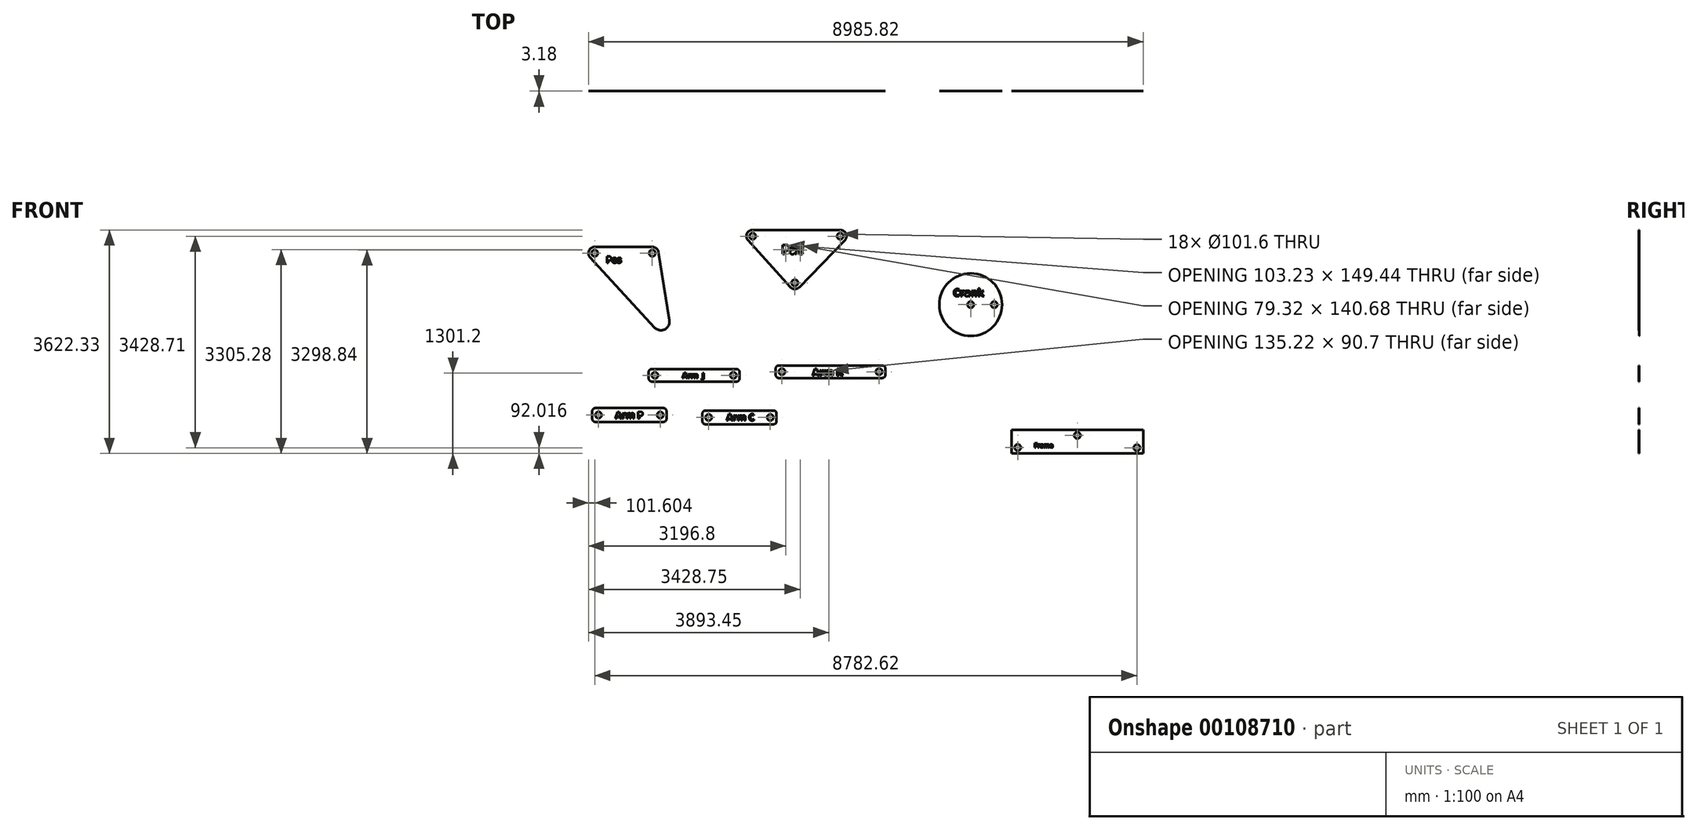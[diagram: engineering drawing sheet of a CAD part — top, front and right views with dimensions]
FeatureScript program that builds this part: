
annotation { "Feature Type Name" : "Feature", "Feature Type Description" : "" }
export const myFeature = defineFeature(function(context is Context, id is Id, definition is map)
    precondition{}
    {
        {
            var Q0;
            Q0=qCreatedBy(makeId("Front.planeOp"),FACE);
            var sketch = newSketch(context, id + "F0", { "sketchPlane" : qUnion([Q0])});
            skLineSegment(sketch, "E0", {"start": v(-44.34, 0) * mm, "end": v(-241.1, 1228.95) * mm, "construction": true});
            skLineSegment(sketch, "E1", {"start": v(-241.1, 1228.95) * mm, "end": v(-1173.29, 1228.95) * mm, "construction": true});
            skLineSegment(sketch, "E2", {"start": v(-1173.29, 1228.95) * mm, "end": v(-44.34, 0) * mm, "construction": true});
            skLineSegment(sketch, "E3", {"start": v(-140.78, 1245.01) * mm, "end": v(35.95, 141.16) * mm});
            skLineSegment(sketch, "E4", {"start": v(-241.1, 1330.55) * mm, "end": v(-1173.29, 1330.55) * mm});
            skLineSegment(sketch, "E5", {"start": v(-1248.1, 1160.21) * mm, "end": v(-204.87, 24.57) * mm});
            skCircle(sketch, "E6", {"center": v(-1173.29, 1228.95) * mm, "radius": 50.8 * mm});
            skCircle(sketch, "E7", {"center": v(-241.1, 1228.95) * mm, "radius": 50.8 * mm});
            skPoint(sketch, "E8.visualSharp", {"position": v(-1404.58, 1330.55) * mm});
            skArc(sketch, "E8.filletArc", {"start": v(-1173.29, 1330.55) * mm, "mid": v(-1266.3, 1269.8) * mm, "end": v(-1248.1, 1160.21) * mm});
            skPoint(sketch, "E9.visualSharp", {"position": v(-154.48, 1330.55) * mm});
            skArc(sketch, "E9.filletArc", {"start": v(-140.78, 1245.01) * mm, "mid": v(-175.19, 1306.26) * mm, "end": v(-241.1, 1330.55) * mm});
            skPoint(sketch, "E10.visualSharp", {"position": v(109.4, -317.53) * mm});
            skArc(sketch, "E10.filletArc", {"start": v(-204.87, 24.57) * mm, "mid": v(-41.12, -6.66) * mm, "end": v(35.95, 141.16) * mm});
            skText(sketch, "E11", { "text": "Pes", "fontName": "OpenSans-Bold.ttf"});
            const initialGuessF0  = {"E11": [-0.98944, 1.07226, 1, 0, 0.10494]};
            skSetInitialGuess(sketch, initialGuessF0);
            skSolve(sketch);
        }
        {
            var Q0;
            Q0=makeQuery(id+"F0.imprint","IMPRINT",FACE,{"disambiguationData":[TD([[makeQuery(id+"F0.imprint","IMPRINT",EDGE,{"derivedFrom":sQuery(id+"F0.wireOp",EDGE,"E3")}),-1.0]])]});
            extrude(context, id + "F1", {"entities" : qUnion([Q0]), "depth" : 3.17 * mm});
        }
        {
            var Q0;
            Q0=qCreatedBy(makeId("Front.planeOp"),FACE);
            var sketch = newSketch(context, id + "F2", { "sketchPlane" : qUnion([Q0])});
            skLineSegment(sketch, "E12", {"start": v(2067.64, 748.14) * mm, "end": v(2802.3, 1504.05) * mm, "construction": true});
            skLineSegment(sketch, "E13", {"start": v(2802.3, 1504.05) * mm, "end": v(1384.98, 1504.05) * mm, "construction": true});
            skLineSegment(sketch, "E14", {"start": v(1384.98, 1504.05) * mm, "end": v(2067.64, 748.14) * mm, "construction": true});
            skLineSegment(sketch, "E15", {"start": v(2875.16, 1433.24) * mm, "end": v(2140.5, 677.33) * mm});
            skLineSegment(sketch, "E16", {"start": v(2802.3, 1605.65) * mm, "end": v(1384.98, 1605.65) * mm});
            skLineSegment(sketch, "E17", {"start": v(1309.58, 1435.95) * mm, "end": v(1992.24, 680.04) * mm});
            skCircle(sketch, "E18", {"center": v(1384.98, 1504.05) * mm, "radius": 50.8 * mm});
            skCircle(sketch, "E19", {"center": v(2802.3, 1504.05) * mm, "radius": 50.8 * mm});
            skPoint(sketch, "E20.visualSharp", {"position": v(1156.33, 1605.65) * mm});
            skArc(sketch, "E20.filletArc", {"start": v(1384.98, 1605.65) * mm, "mid": v(1292.14, 1545.3) * mm, "end": v(1309.58, 1435.95) * mm});
            skPoint(sketch, "E21.visualSharp", {"position": v(3042.73, 1605.65) * mm});
            skArc(sketch, "E21.filletArc", {"start": v(2875.16, 1433.24) * mm, "mid": v(2895.89, 1543.6) * mm, "end": v(2802.3, 1605.65) * mm});
            skPoint(sketch, "E22.visualSharp", {"position": v(2064.92, 599.56) * mm});
            skArc(sketch, "E22.filletArc", {"start": v(1992.24, 680.04) * mm, "mid": v(2065.78, 646.56) * mm, "end": v(2140.5, 677.33) * mm});
            skCircle(sketch, "E23", {"center": v(2067.64, 748.14) * mm, "radius": 50.8 * mm});
            skText(sketch, "E24", { "text": "Pat", "fontName": "OpenSans-Bold.ttf"});
            const initialGuessF2  = {"E24": [1.85149, 1.21388, 1, 0, 0.15072]};
            skSetInitialGuess(sketch, initialGuessF2);
            skSolve(sketch);
        }
        {
            var Q0;
            Q0=makeQuery(id+"F2.imprint","IMPRINT",FACE,{"disambiguationData":[TD([[makeQuery(id+"F2.imprint","IMPRINT",EDGE,{"derivedFrom":sQuery(id+"F2.wireOp",EDGE,"E15")}),-1.0]])]});
            extrude(context, id + "F3", {"entities" : qUnion([Q0]), "depth" : 3.17 * mm});
        }
        {
            var Q0;
            Q0=qCreatedBy(makeId("Front.planeOp"),FACE);
            var sketch = newSketch(context, id + "F4", { "sketchPlane" : qUnion([Q0])});
            skLineSegment(sketch, "E25.bottom", {"start": v(-248.2, -648.94) * mm, "end": v(1123.4, -648.94) * mm});
            skLineSegment(sketch, "E25.top", {"start": v(-248.2, -852.14) * mm, "end": v(1123.4, -852.14) * mm});
            skLineSegment(sketch, "E25.left", {"start": v(-299, -699.74) * mm, "end": v(-299, -801.34) * mm});
            skLineSegment(sketch, "E25.right", {"start": v(1174.2, -699.74) * mm, "end": v(1174.2, -801.34) * mm});
            skLineSegment(sketch, "E26", {"start": v(-197.4, -750.54) * mm, "end": v(1072.6, -750.54) * mm, "construction": true});
            skPoint(sketch, "E26.startSnap0", {"position": v(-299, -750.54) * mm});
            skPoint(sketch, "E26.endSnap0", {"position": v(1174.2, -750.54) * mm});
            skCircle(sketch, "E27", {"center": v(-197.4, -750.54) * mm, "radius": 50.8 * mm});
            skCircle(sketch, "E28", {"center": v(1072.6, -750.54) * mm, "radius": 50.8 * mm});
            skPoint(sketch, "E29.visualSharp", {"position": v(1174.2, -852.14) * mm});
            skArc(sketch, "E29.filletArc", {"start": v(1123.4, -852.14) * mm, "mid": v(1159.32, -837.26) * mm, "end": v(1174.2, -801.34) * mm});
            skPoint(sketch, "E30.visualSharp", {"position": v(1174.2, -648.94) * mm});
            skArc(sketch, "E30.filletArc", {"start": v(1174.2, -699.74) * mm, "mid": v(1159.32, -663.82) * mm, "end": v(1123.4, -648.94) * mm});
            skPoint(sketch, "E31.visualSharp", {"position": v(-299, -648.94) * mm});
            skArc(sketch, "E31.filletArc", {"start": v(-248.2, -648.94) * mm, "mid": v(-284.13, -663.82) * mm, "end": v(-299, -699.74) * mm});
            skPoint(sketch, "E32.visualSharp", {"position": v(-299, -852.14) * mm});
            skArc(sketch, "E32.filletArc", {"start": v(-299, -801.34) * mm, "mid": v(-284.13, -837.26) * mm, "end": v(-248.2, -852.14) * mm});
            skText(sketch, "E33", { "text": "Arm  J", "fontName": "OpenSans-Bold.ttf"});
            const initialGuessF4  = {"E33": [0.24657, -0.79744, 1, 0, 0.08674]};
            skSetInitialGuess(sketch, initialGuessF4);
            skSolve(sketch);
        }
        {
            var Q0;
            Q0=makeQuery(id+"F4.imprint","IMPRINT",FACE,{"disambiguationData":[TD([[makeQuery(id+"F4.imprint","IMPRINT",EDGE,{"derivedFrom":sQuery(id+"F4.wireOp",EDGE,"E25.bottom")}),-1.0]])]});
            extrude(context, id + "F5", {"entities" : qUnion([Q0]), "depth" : 3.17 * mm});
        }
        {
            var Q0;
            Q0=qCreatedBy(makeId("Front.planeOp"),FACE);
            var sketch = newSketch(context, id + "F6", { "sketchPlane" : qUnion([Q0])});
            skLineSegment(sketch, "E34.bottom", {"start": v(1808.96, -591.1) * mm, "end": v(3482.82, -591.1) * mm});
            skLineSegment(sketch, "E34.top", {"start": v(1808.96, -794.3) * mm, "end": v(3482.82, -794.3) * mm});
            skLineSegment(sketch, "E34.left", {"start": v(1758.16, -641.9) * mm, "end": v(1758.16, -743.5) * mm});
            skLineSegment(sketch, "E34.right", {"start": v(3533.62, -641.9) * mm, "end": v(3533.62, -743.5) * mm});
            skLineSegment(sketch, "E35", {"start": v(1859.76, -692.7) * mm, "end": v(3432.02, -692.7) * mm, "construction": true});
            skPoint(sketch, "E35.startSnap0", {"position": v(1758.16, -692.7) * mm});
            skPoint(sketch, "E35.endSnap0", {"position": v(3533.62, -692.7) * mm});
            skCircle(sketch, "E36", {"center": v(1859.76, -692.7) * mm, "radius": 50.8 * mm});
            skCircle(sketch, "E37", {"center": v(3432.02, -692.7) * mm, "radius": 50.8 * mm});
            skPoint(sketch, "E38.visualSharp", {"position": v(3533.62, -794.3) * mm});
            skArc(sketch, "E38.filletArc", {"start": v(3482.82, -794.3) * mm, "mid": v(3518.74, -779.42) * mm, "end": v(3533.62, -743.5) * mm});
            skPoint(sketch, "E39.visualSharp", {"position": v(3533.62, -591.1) * mm});
            skArc(sketch, "E39.filletArc", {"start": v(3533.62, -641.9) * mm, "mid": v(3518.74, -605.98) * mm, "end": v(3482.82, -591.1) * mm});
            skPoint(sketch, "E40.visualSharp", {"position": v(1758.16, -591.1) * mm});
            skArc(sketch, "E40.filletArc", {"start": v(1808.96, -591.1) * mm, "mid": v(1773.04, -605.98) * mm, "end": v(1758.16, -641.9) * mm});
            skPoint(sketch, "E41.visualSharp", {"position": v(1758.16, -794.3) * mm});
            skArc(sketch, "E41.filletArc", {"start": v(1758.16, -743.5) * mm, "mid": v(1773.04, -779.42) * mm, "end": v(1808.96, -794.3) * mm});
            skText(sketch, "E42", { "text": "Arm K", "fontName": "OpenSans-Bold.ttf"});
            const initialGuessF6  = {"E42": [2.35162, -0.76083, 1, 0, 0.11743]};
            skSetInitialGuess(sketch, initialGuessF6);
            skSolve(sketch);
        }
        {
            var Q0;
            Q0=qCreatedBy(makeId("Front.planeOp"),FACE);
            var sketch = newSketch(context, id + "F7", { "sketchPlane" : qUnion([Q0])});
            skLineSegment(sketch, "E43.bottom", {"start": v(-1163, -1282.62) * mm, "end": v(-60.65, -1282.62) * mm});
            skLineSegment(sketch, "E43.top", {"start": v(-1163, -1506.74) * mm, "end": v(-60.65, -1506.74) * mm});
            skLineSegment(sketch, "E43.left", {"start": v(-1213.8, -1333.42) * mm, "end": v(-1213.8, -1455.94) * mm});
            skLineSegment(sketch, "E43.right", {"start": v(-9.85, -1333.42) * mm, "end": v(-9.85, -1455.94) * mm});
            skLineSegment(sketch, "E44", {"start": v(-1112.2, -1394.68) * mm, "end": v(-111.45, -1394.68) * mm, "construction": true});
            skPoint(sketch, "E44.startSnap0", {"position": v(-1213.8, -1394.68) * mm});
            skPoint(sketch, "E44.endSnap0", {"position": v(-9.85, -1394.68) * mm});
            skCircle(sketch, "E45", {"center": v(-1112.2, -1394.68) * mm, "radius": 50.8 * mm});
            skCircle(sketch, "E46", {"center": v(-111.45, -1394.68) * mm, "radius": 50.8 * mm});
            skPoint(sketch, "E47.visualSharp", {"position": v(-9.85, -1506.74) * mm});
            skArc(sketch, "E47.filletArc", {"start": v(-60.65, -1506.74) * mm, "mid": v(-24.73, -1491.86) * mm, "end": v(-9.85, -1455.94) * mm});
            skPoint(sketch, "E48.visualSharp", {"position": v(-9.85, -1282.62) * mm});
            skArc(sketch, "E48.filletArc", {"start": v(-9.85, -1333.42) * mm, "mid": v(-24.73, -1297.5) * mm, "end": v(-60.65, -1282.62) * mm});
            skPoint(sketch, "E49.visualSharp", {"position": v(-1213.8, -1282.62) * mm});
            skArc(sketch, "E49.filletArc", {"start": v(-1163, -1282.62) * mm, "mid": v(-1198.93, -1297.5) * mm, "end": v(-1213.8, -1333.42) * mm});
            skPoint(sketch, "E50.visualSharp", {"position": v(-1213.8, -1506.74) * mm});
            skArc(sketch, "E50.filletArc", {"start": v(-1213.8, -1455.94) * mm, "mid": v(-1198.93, -1491.86) * mm, "end": v(-1163, -1506.74) * mm});
            skText(sketch, "E51", { "text": "Arm P", "fontName": "OpenSans-Bold.ttf"});
            const initialGuessF7  = {"E51": [-0.84316, -1.44791, 1, 0, 0.10851]};
            skSetInitialGuess(sketch, initialGuessF7);
            skSolve(sketch);
        }
        {
            var Q0;
            Q0=qCreatedBy(makeId("Front.planeOp"),FACE);
            var sketch = newSketch(context, id + "F8", { "sketchPlane" : qUnion([Q0])});
            skLineSegment(sketch, "E52.bottom", {"start": v(621.11, -1321.32) * mm, "end": v(1720.93, -1321.32) * mm});
            skLineSegment(sketch, "E52.top", {"start": v(621.11, -1545.44) * mm, "end": v(1720.93, -1545.44) * mm});
            skLineSegment(sketch, "E52.left", {"start": v(570.31, -1372.12) * mm, "end": v(570.31, -1494.64) * mm});
            skLineSegment(sketch, "E52.right", {"start": v(1771.73, -1372.12) * mm, "end": v(1771.73, -1494.64) * mm});
            skLineSegment(sketch, "E53", {"start": v(671.91, -1433.38) * mm, "end": v(1670.13, -1433.38) * mm, "construction": true});
            skPoint(sketch, "E53.startSnap0", {"position": v(570.31, -1433.38) * mm});
            skPoint(sketch, "E53.endSnap0", {"position": v(1771.73, -1433.38) * mm});
            skCircle(sketch, "E54", {"center": v(671.91, -1433.38) * mm, "radius": 50.8 * mm});
            skCircle(sketch, "E55", {"center": v(1670.13, -1433.38) * mm, "radius": 50.8 * mm});
            skPoint(sketch, "E56.visualSharp", {"position": v(1771.73, -1545.44) * mm});
            skArc(sketch, "E56.filletArc", {"start": v(1720.93, -1545.44) * mm, "mid": v(1756.85, -1530.56) * mm, "end": v(1771.73, -1494.64) * mm});
            skPoint(sketch, "E57.visualSharp", {"position": v(1771.73, -1321.32) * mm});
            skArc(sketch, "E57.filletArc", {"start": v(1771.73, -1372.12) * mm, "mid": v(1756.85, -1336.2) * mm, "end": v(1720.93, -1321.32) * mm});
            skPoint(sketch, "E58.visualSharp", {"position": v(570.31, -1321.32) * mm});
            skArc(sketch, "E58.filletArc", {"start": v(621.11, -1321.32) * mm, "mid": v(585.2, -1336.2) * mm, "end": v(570.31, -1372.12) * mm});
            skPoint(sketch, "E59.visualSharp", {"position": v(570.31, -1545.44) * mm});
            skArc(sketch, "E59.filletArc", {"start": v(570.31, -1494.64) * mm, "mid": v(585.2, -1530.56) * mm, "end": v(621.11, -1545.44) * mm});
            skText(sketch, "E60", { "text": "Arm C", "fontName": "OpenSans-Bold.ttf"});
            const initialGuessF8  = {"E60": [0.96125, -1.4849, 1, 0, 0.10784]};
            skSetInitialGuess(sketch, initialGuessF8);
            skSolve(sketch);
        }
        {
            var Q0;
            Q0 = qSketchRegion(id + "F6", true);
            extrude(context, id + "F9", {"entities" : qUnion([Q0]), "depth" : 3.17 * mm});
        }
        {
            var Q0;
            Q0 = qSketchRegion(id + "F7", true);
            extrude(context, id + "F10", {"entities" : qUnion([Q0]), "depth" : 3.17 * mm});
        }
        {
            var Q0;
            Q0 = qSketchRegion(id + "F8", true);
            extrude(context, id + "F11", {"entities" : qUnion([Q0]), "depth" : 3.17 * mm});
        }
        {
            var Q0;
            Q0=qCreatedBy(makeId("Front.planeOp"),FACE);
            var sketch = newSketch(context, id + "F12", { "sketchPlane" : qUnion([Q0])});
            skCircle(sketch, "E61", {"center": v(4917.26, 394.5) * mm, "radius": 508 * mm});
            skCircle(sketch, "E62", {"center": v(4917.26, 394.5) * mm, "radius": 50.8 * mm});
            skCircle(sketch, "E63", {"center": v(5298.26, 394.5) * mm, "radius": 50.8 * mm});
            skText(sketch, "E64", { "text": "Crank", "fontName": "OpenSans-Bold.ttf"});
            const initialGuessF12  = {"E64": [4.6341, 0.52902, 1, 0, 0.12041]};
            skSetInitialGuess(sketch, initialGuessF12);
            skSolve(sketch);
        }
        {
            var Q0;
            Q0=makeQuery(id+"F12.imprint","IMPRINT",FACE,{"disambiguationData":[TD([[makeQuery(id+"F12.imprint","IMPRINT",EDGE,{"derivedFrom":sQuery(id+"F12.wireOp",EDGE,"E61")}),1.0]])]});
            extrude(context, id + "F13", {"entities" : qUnion([Q0]), "depth" : 0.32 * mm});
        }
        {
            var Q0;
            Q0=qCreatedBy(makeId("Front.planeOp"),FACE);
            var sketch = newSketch(context, id + "F14", { "sketchPlane" : qUnion([Q0])});
            skLineSegment(sketch, "E65.bottom", {"start": v(5577.33, -1635.68) * mm, "end": v(7710.93, -1635.68) * mm});
            skLineSegment(sketch, "E65.top", {"start": v(5577.33, -2016.68) * mm, "end": v(7710.93, -2016.68) * mm});
            skLineSegment(sketch, "E65.left", {"start": v(5577.33, -1635.68) * mm, "end": v(5577.33, -2016.68) * mm});
            skLineSegment(sketch, "E65.right", {"start": v(7710.93, -1635.68) * mm, "end": v(7710.93, -2016.68) * mm});
            skPoint(sketch, "E66.centerSnap0", {"position": v(6644.13, -1635.68) * mm});
            skCircle(sketch, "E67", {"center": v(5678.93, -1921.08) * mm, "radius": 50.8 * mm});
            skCircle(sketch, "E68", {"center": v(7609.33, -1924.66) * mm, "radius": 50.8 * mm});
            skCircle(sketch, "E69", {"center": v(6644.13, -1724.75) * mm, "radius": 50.8 * mm});
            skLineSegment(sketch, "E70", {"start": v(5678.93, -1921.08) * mm, "end": v(7609.33, -1924.66) * mm, "construction": true});
            skLineSegment(sketch, "E71", {"start": v(6644.13, -1635.68) * mm, "end": v(6644.13, -2016.68) * mm, "construction": true});
            skText(sketch, "E72", { "text": "Frame", "fontName": "OpenSans-Bold.ttf"});
            const initialGuessF14  = {"E72": [5.94753, -1.92214, 1, 0, 0.06855]};
            skSetInitialGuess(sketch, initialGuessF14);
            skSolve(sketch);
        }
        {
            var Q0;
            Q0=makeQuery(id+"F14.imprint","IMPRINT",FACE,{"disambiguationData":[TD([[makeQuery(id+"F14.imprint","IMPRINT",EDGE,{"derivedFrom":sQuery(id+"F14.wireOp",EDGE,"E65.bottom")}),-1.0]])]});
            extrude(context, id + "F15", {"entities" : qUnion([Q0]), "depth" : 3.17 * mm});
        }
    });
